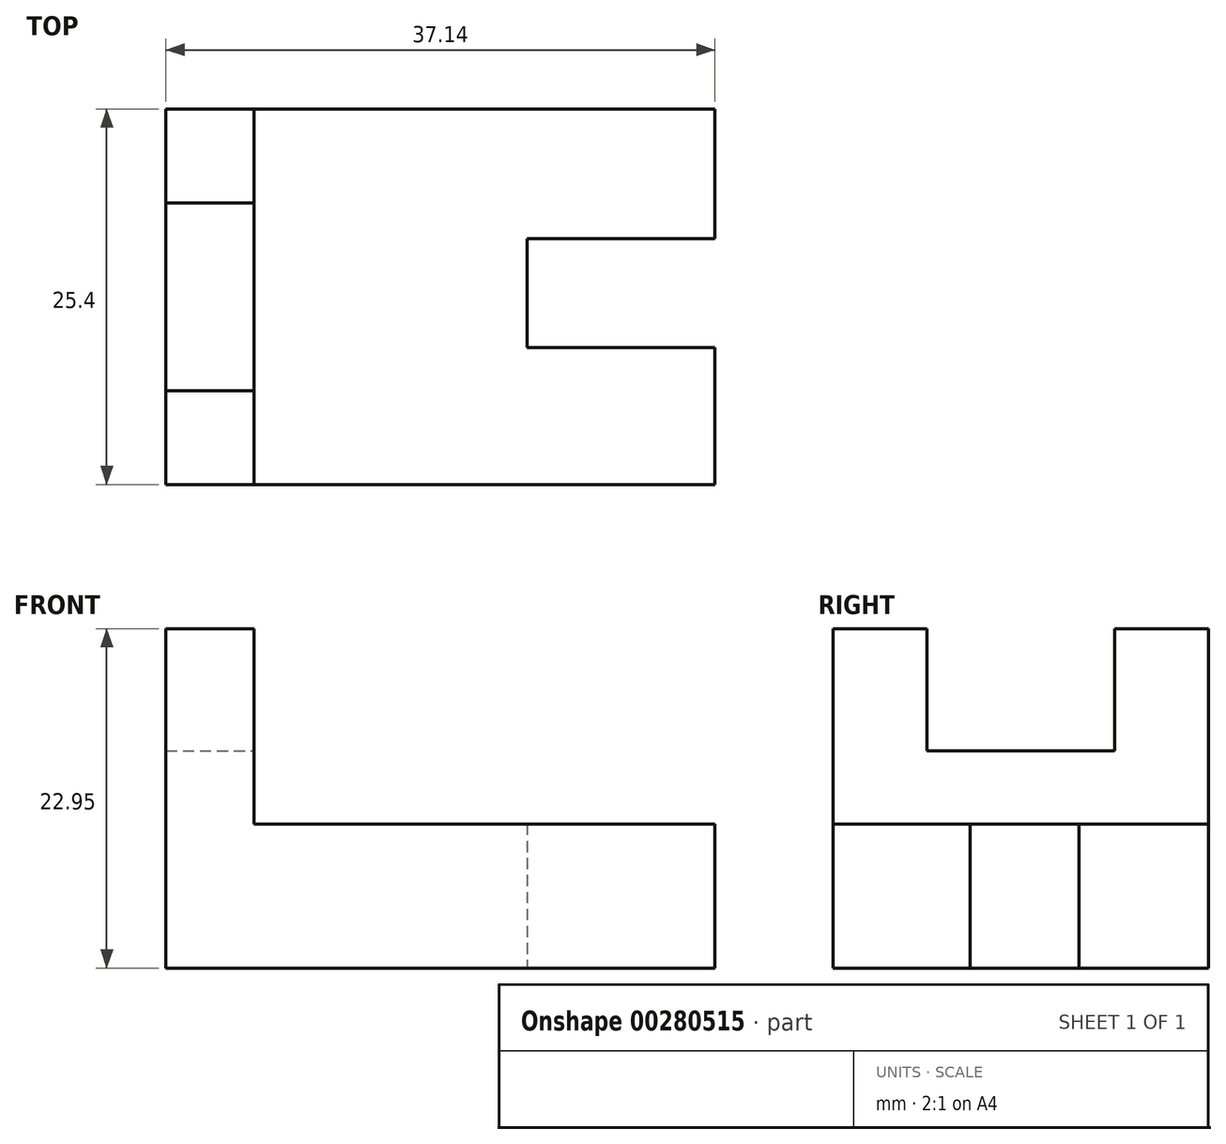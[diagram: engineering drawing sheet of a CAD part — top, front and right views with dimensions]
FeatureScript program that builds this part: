
annotation { "Feature Type Name" : "Feature", "Feature Type Description" : "" }
export const myFeature = defineFeature(function(context is Context, id is Id, definition is map)
    precondition{}
    {
        {
            var Q0;
            Q0=qCreatedBy(makeId("Front.planeOp"),FACE);
            var sketch = newSketch(context, id + "F0", { "sketchPlane" : qUnion([Q0])});
            skLineSegment(sketch, "E0", {"start": v(0, 0) * mm, "end": v(0, 22.95) * mm});
            skLineSegment(sketch, "E1", {"start": v(0, 22.95) * mm, "end": v(5.95, 22.95) * mm});
            skLineSegment(sketch, "E2", {"start": v(5.95, 22.95) * mm, "end": v(5.95, 9.74) * mm});
            skLineSegment(sketch, "E3", {"start": v(5.95, 9.74) * mm, "end": v(37.14, 9.74) * mm});
            skLineSegment(sketch, "E4", {"start": v(37.14, 9.74) * mm, "end": v(37.14, 0) * mm});
            skLineSegment(sketch, "E5", {"start": v(37.14, 0) * mm, "end": v(0, 0) * mm});
            skSolve(sketch);
        }
        {
            var Q0;
            Q0 = qSketchRegion(id + "F0", true);
            extrude(context, id + "F1", {"entities" : qUnion([Q0]), "depth" : 25.4 * mm});
        }
        {
            var Q0;
            Q0=makeQuery(id+"F1.opExtrude","SWEPT_FACE",FACE,{"disambiguationData":[OSD([sQuery(id+"F0.wireOp",EDGE,"E1")])]});
            var sketch = newSketch(context, id + "F2", { "sketchPlane" : qUnion([Q0])});
            skLineSegment(sketch, "E6", {"start": v(0, -19.05) * mm, "end": v(5.95, -19.05) * mm});
            skLineSegment(sketch, "E7", {"start": v(5.95, -19.05) * mm, "end": v(5.95, -6.35) * mm});
            skLineSegment(sketch, "E8", {"start": v(5.95, -6.35) * mm, "end": v(0, -6.35) * mm});
            skLineSegment(sketch, "E9", {"start": v(0, -6.35) * mm, "end": v(0, -19.05) * mm});
            skSolve(sketch);
        }
        {
            var Q0;
            Q0 = qSketchRegion(id + "F2", true);
            extrude(context, id + "F3", {"entities" : qUnion([Q0]), "operationType" : NewBodyOperationType.REMOVE, "endBound" : BoundingType.SYMMETRIC, "oppositeDirection" : true, "depth" : 16.5 * mm});
        }
        {
            var Q0;
            Q0=makeQuery(id+"F1.opExtrude","SWEPT_FACE",FACE,{"disambiguationData":[OSD([sQuery(id+"F0.wireOp",EDGE,"E4")])]});
            var sketch = newSketch(context, id + "F4", { "sketchPlane" : qUnion([Q0])});
            skLineSegment(sketch, "E10", {"start": v(-16.13, 9.74) * mm, "end": v(-16.13, 0) * mm});
            skLineSegment(sketch, "E11", {"start": v(-16.13, 0) * mm, "end": v(-8.77, 0) * mm});
            skLineSegment(sketch, "E12", {"start": v(-8.77, 0) * mm, "end": v(-8.77, 9.74) * mm});
            skLineSegment(sketch, "E13", {"start": v(-8.77, 9.74) * mm, "end": v(-16.13, 9.74) * mm});
            skSolve(sketch);
        }
        {
            var Q0;
            Q0 = qSketchRegion(id + "F4", true);
            extrude(context, id + "F5", {"entities" : qUnion([Q0]), "operationType" : NewBodyOperationType.REMOVE, "endBound" : BoundingType.SYMMETRIC, "oppositeDirection" : true, "depth" : 25.4 * mm});
        }
    });
